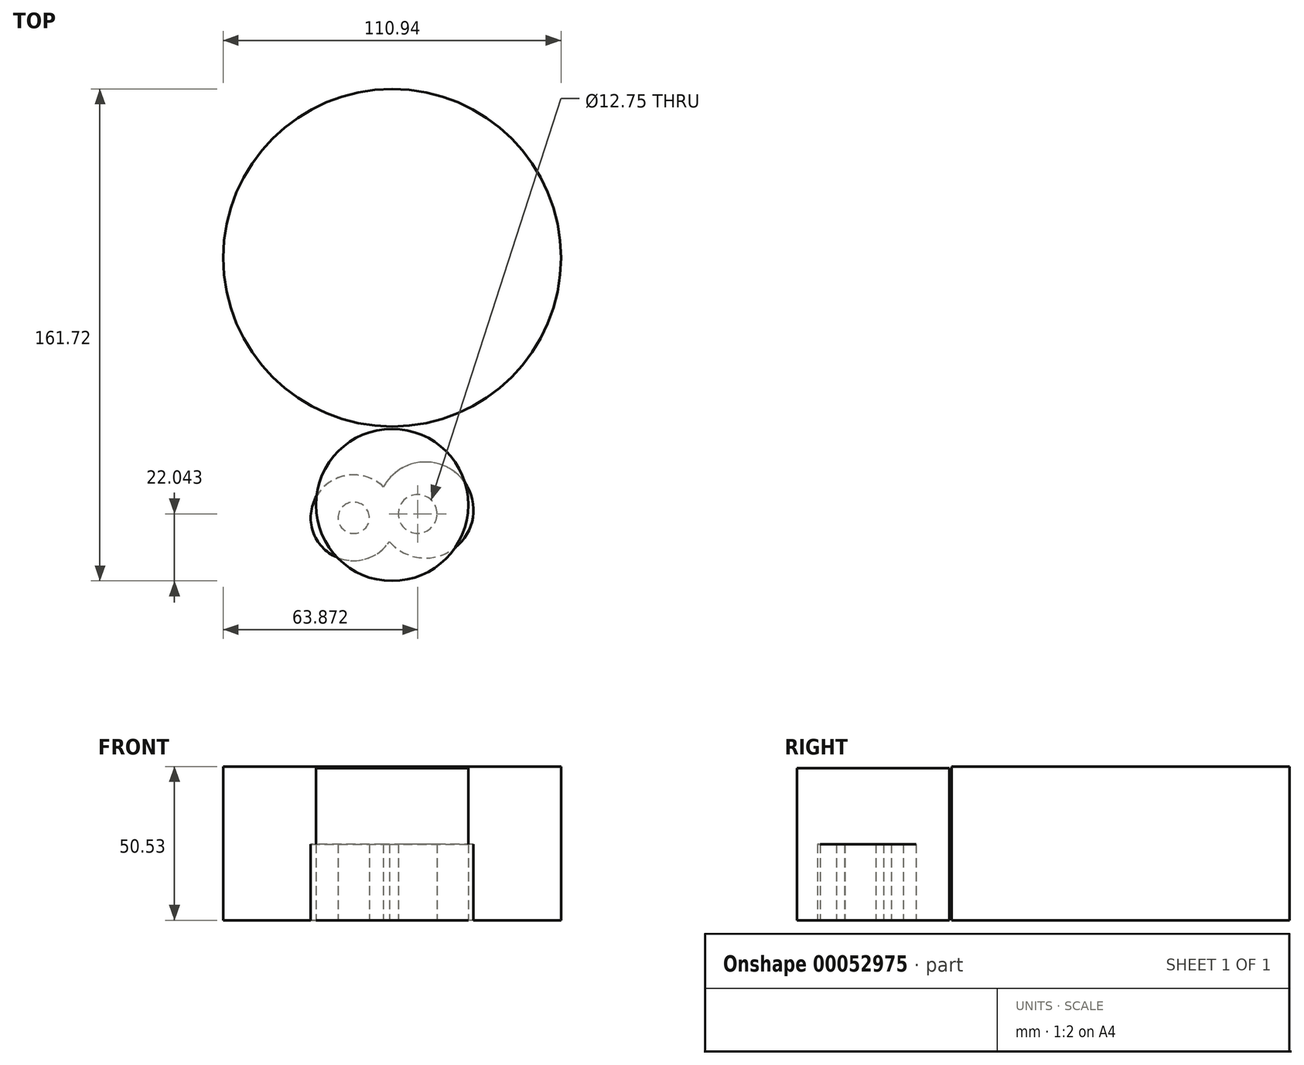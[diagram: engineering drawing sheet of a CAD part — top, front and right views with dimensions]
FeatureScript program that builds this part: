
annotation { "Feature Type Name" : "Feature", "Feature Type Description" : "" }
export const myFeature = defineFeature(function(context is Context, id is Id, definition is map)
    precondition{}
    {
        {
            var Q0;
            Q0=qCreatedBy(makeId("Top.planeOp"),FACE);
            var sketch = newSketch(context, id + "F0", { "sketchPlane" : qUnion([Q0])});
            skCircle(sketch, "E0", {"center": v(0, -68.06) * mm, "radius": 25 * mm});
            skSolve(sketch);
        }
        {
            var Q0;
            Q0=makeQuery(id+"F0.imprint","IMPRINT",FACE,{"disambiguationData":[TD([[makeQuery(id+"F0.imprint","IMPRINT",EDGE,{"derivedFrom":sQuery(id+"F0.wireOp",EDGE,"E0")}),1.0]])]});
            var sketch = newSketch(context, id + "F1", { "sketchPlane" : qUnion([Q0])});
            skSolve(sketch);
        }
        {
            var Q0;
            Q0 = qSketchRegion(id + "F1", true);
            var Q1;
            Q1=makeQuery(id+"F1.imprint","IMPRINT",FACE,{"disambiguationData":[TD([[makeQuery(id+"F1.imprint","IMPRINT",EDGE,{"derivedFrom":makeQuery(id+"F0.imprint","IMPRINT",EDGE,{"derivedFrom":sQuery(id+"F0.wireOp",EDGE,"E0")})}),1.0]])]});
            var Q2;
            Q2=makeQuery(id+"F0.imprint","IMPRINT",FACE,{"disambiguationData":[TD([[makeQuery(id+"F0.imprint","IMPRINT",EDGE,{"derivedFrom":sQuery(id+"F0.wireOp",EDGE,"E0")}),1.0]])]});
            extrude(context, id + "F2", {"entities" : qUnion([Q0, Q1, Q2]), "depth" : 50 * mm});
        }
        {
            var Q0;
            Q0=qCreatedBy(makeId("Top.planeOp"),FACE);
            var sketch = newSketch(context, id + "F3", { "sketchPlane" : qUnion([Q0])});
            skCircle(sketch, "E1", {"center": v(0, 13.2) * mm, "radius": 55.47 * mm});
            skSolve(sketch);
        }
        {
            var Q0;
            Q0=makeQuery(id+"F3.imprint","IMPRINT",FACE,{"disambiguationData":[TD([[makeQuery(id+"F3.imprint","IMPRINT",EDGE,{"derivedFrom":sQuery(id+"F3.wireOp",EDGE,"E1")}),1.0]])]});
            extrude(context, id + "F4", {"entities" : qUnion([Q0]), "depth" : 37.87 * mm});
        }
        {
            var Q0;
            Q0=qCreatedBy(makeId("Top.planeOp"),FACE);
            var sketch = newSketch(context, id + "F5", { "sketchPlane" : qUnion([Q0])});
            skCircle(sketch, "E2", {"center": v(-12.63, -72.3) * mm, "radius": 5.14 * mm});
            skCircle(sketch, "E3", {"center": v(8.4, -71.02) * mm, "radius": 6.37 * mm});
            skCircle(sketch, "E4", {"center": v(-12.63, -72.3) * mm, "radius": 14.1 * mm});
            skCircle(sketch, "E5", {"center": v(10.95, -69.74) * mm, "radius": 15.78 * mm});
            skSolve(sketch);
        }
        {
            var Q0;
            Q0 = qSketchRegion(id + "F5", true);
            extrude(context, id + "F6", {"entities" : qUnion([Q0]), "depth" : 25 * mm});
        }
        {
            var Q0;
            Q0=makeQuery(id+"F4.opExtrude","CAP_FACE",FACE,{"disambiguationData":[OSD([sQuery(id+"F3.wireOp",EDGE,"E1")])],"isStart":true});
            extrude(context, id + "F7", {"entities" : qUnion([Q0]), "operationType" : NewBodyOperationType.ADD, "oppositeDirection" : true, "depth" : 50.53 * mm});
        }
    });
